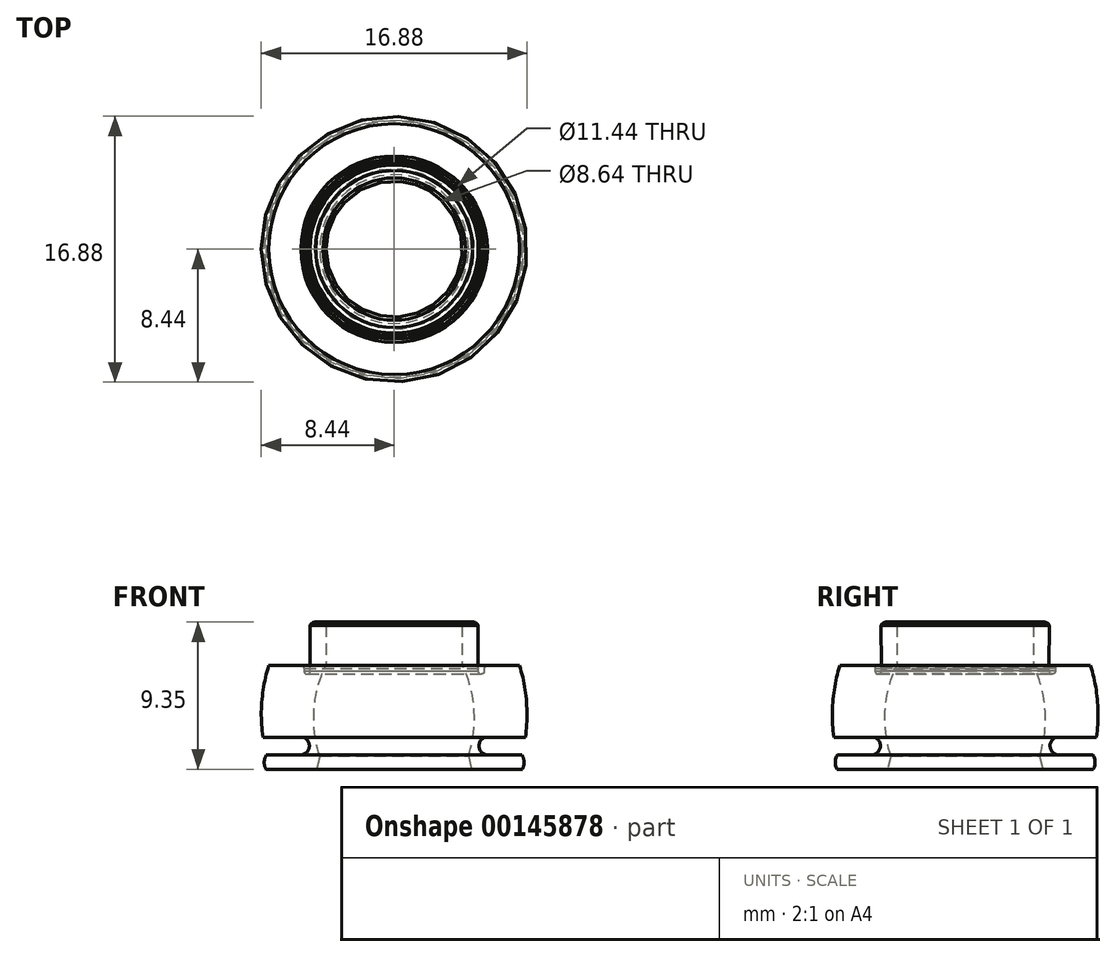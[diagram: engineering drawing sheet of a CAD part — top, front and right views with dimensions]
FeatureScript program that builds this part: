
annotation { "Feature Type Name" : "Feature", "Feature Type Description" : "" }
export const myFeature = defineFeature(function(context is Context, id is Id, definition is map)
    precondition{}
    {
        {
            var Q0;
            Q0=qCreatedBy(makeId("Front.planeOp"),FACE);
            var sketch = newSketch(context, id + "F0", { "sketchPlane" : qUnion([Q0])});
            skLineSegment(sketch, "E0", {"start": v(-10.48, -0.16) * mm, "end": v(-14.05, -0.16) * mm, "construction": true});
            skLineSegment(sketch, "E1", {"start": v(-14.05, 0.64) * mm, "end": v(-10.5, 0.64) * mm, "construction": true});
            skLineSegment(sketch, "E2", {"start": v(-14.05, 2.04) * mm, "end": v(-10.5, 2.04) * mm, "construction": true});
            skLineSegment(sketch, "E3", {"start": v(-10.5, 6.64) * mm, "end": v(-14.05, 6.64) * mm, "construction": true});
            skLineSegment(sketch, "E4", {"start": v(-10.5, 9.34) * mm, "end": v(-14.05, 9.34) * mm, "construction": true});
            skLineSegment(sketch, "E5", {"start": v(-8.1, 0.9) * mm, "end": v(-5.88, 0.9) * mm});
            skPoint(sketch, "E6.endSnap0", {"position": v(-10.51, 4.48) * mm});
            skLineSegment(sketch, "E7", {"start": v(-4.3, 9.15) * mm, "end": v(-4.3, 6.64) * mm});
            skPoint(sketch, "E8", {"position": v(-5.36, 4.42) * mm});
            skPoint(sketch, "E9.visualSharp", {"position": v(-5.36, 2.2) * mm});
            skPoint(sketch, "E10.visualSharp", {"position": v(-5.31, 6.6) * mm});
            skPoint(sketch, "E11.visualSharp", {"position": v(-7.3, 0.86) * mm});
            skLineSegment(sketch, "E12", {"start": v(0.02, -117.65) * mm, "end": v(0.02, -111.65) * mm});
            skLineSegment(sketch, "E13", {"start": v(-8.43, 9.56) * mm, "end": v(-8.43, 0.56) * mm, "construction": true});
            skPoint(sketch, "E13.startSnap0", {"position": v(-8.43, 4.42) * mm});
            skPoint(sketch, "E9.filletArc.center.orphan", {"position": v(-5.4, 2.04) * mm});
            skPoint(sketch, "E14.visualSharp", {"position": v(-5.17, 9.35) * mm});
            skPoint(sketch, "E15.visualSharp", {"position": v(-4.3, 9.35) * mm});
            skArc(sketch, "E15.filletArc", {"start": v(-4.3, 9.15) * mm, "mid": v(-4.36, 9.3) * mm, "end": v(-4.5, 9.35) * mm});
            skLineSegment(sketch, "E16", {"start": v(-8.32, 2.04) * mm, "end": v(-5.74, 2.04) * mm});
            skArc(sketch, "E17", {"start": v(-7.94, 6.61) * mm, "mid": v(-8.38, 4.35) * mm, "end": v(-8.32, 2.04) * mm});
            skLineSegment(sketch, "E18", {"start": v(-8.12, 0) * mm, "end": v(-4.9, 0) * mm});
            skLineSegment(sketch, "E19", {"start": v(-7.94, 6.61) * mm, "end": v(-5.9, 6.61) * mm});
            skLineSegment(sketch, "E20", {"start": v(-5.7, 6.41) * mm, "end": v(-5.7, 6.25) * mm});
            skLineSegment(sketch, "E21", {"start": v(-5.51, 6.05) * mm, "end": v(-5.5, 6.05) * mm});
            skPoint(sketch, "E22.visualSharp", {"position": v(-5.7, 6.61) * mm});
            skArc(sketch, "E22.filletArc", {"start": v(-5.7, 6.41) * mm, "mid": v(-5.77, 6.55) * mm, "end": v(-5.9, 6.61) * mm});
            skLineSegment(sketch, "E23", {"start": v(-5.31, 6.25) * mm, "end": v(-5.32, 9.15) * mm});
            skPoint(sketch, "E24.visualSharp", {"position": v(-5.7, 6.05) * mm});
            skArc(sketch, "E24.filletArc", {"start": v(-5.7, 6.25) * mm, "mid": v(-5.65, 6.1) * mm, "end": v(-5.5, 6.05) * mm});
            skPoint(sketch, "E25.visualSharp", {"position": v(-5.31, 6.05) * mm});
            skArc(sketch, "E25.filletArc", {"start": v(-5.51, 6.05) * mm, "mid": v(-5.37, 6.1) * mm, "end": v(-5.31, 6.25) * mm});
            skArc(sketch, "E26", {"start": v(-4.3, 6.64) * mm, "mid": v(-5.06, 3.78) * mm, "end": v(-4.7, 0.84) * mm});
            skLineSegment(sketch, "E27", {"start": v(-4.97, 9.35) * mm, "end": v(-4.5, 9.35) * mm});
            skArc(sketch, "E28", {"start": v(-5.88, 0.9) * mm, "mid": v(-5.37, 1.42) * mm, "end": v(-5.74, 2.04) * mm});
            skArc(sketch, "E29", {"start": v(-8.1, 0.9) * mm, "mid": v(-8.23, 0.46) * mm, "end": v(-8.12, 0) * mm});
            skArc(sketch, "E30", {"start": v(-4.97, 9.35) * mm, "mid": v(-5.17, 9.3) * mm, "end": v(-5.32, 9.15) * mm});
            skPoint(sketch, "E31", {"position": v(-5.08, 3.33) * mm});
            skLineSegment(sketch, "E32", {"start": v(0, 0) * mm, "end": v(0, 10.46) * mm});
            skLineSegment(sketch, "E33", {"start": v(-4.9, 0) * mm, "end": v(-4.7, 0.84) * mm});
            skSolve(sketch);
        }
        {
            var Q0;
            Q0=makeQuery(id+"F0.imprint","IMPRINT",FACE,{"disambiguationData":[TD([[makeQuery(id+"F0.imprint","IMPRINT",EDGE,{"derivedFrom":sQuery(id+"F0.wireOp",EDGE,"7BqM3D1l-dlXT-mzmC-aZGA-8GqCBN6UsZia")}),-1.0]])]});
            var Q1;
            Q1=makeQuery(id+"F0.imprint","IMPRINT",FACE,{"disambiguationData":[TD([[makeQuery(id+"F0.imprint","IMPRINT",EDGE,{"derivedFrom":sQuery(id+"F0.wireOp",EDGE,"E5")}),-1.0]])]});
            var Q2;
            Q2=sQuery(id+"F0.wireOp",EDGE,"E12");
            revolve(context, id + "F1", {"entities" : qUnion([Q0, Q1]), "axis" : qUnion([Q2]), "revolveType" : RevolveType.FULL});
        }
        {
            var Q0;
            Q0=makeQuery(id+"F1.opRevolve","SWEPT_BODY",BODY,{"disambiguationData":[OSD([sQuery(id+"F0.wireOp",EDGE,"LSrZbnCW-DPXI-OJCB-wGV7-goqquTMaoNQ3"),sQuery(id+"F0.wireOp",EDGE,"E5"),sQuery(id+"F0.wireOp",EDGE,"q9hycEio-vNRm-B8LW-tvsp-It3O9ZgXLD7L"),sQuery(id+"F0.wireOp",EDGE,"E7"),sQuery(id+"F0.wireOp",EDGE,"E11.filletArc"),sQuery(id+"F0.wireOp",EDGE,"E14.filletArc"),sQuery(id+"F0.wireOp",EDGE,"E15.filletArc"),sQuery(id+"F0.wireOp",EDGE,"E16"),sQuery(id+"F0.wireOp",EDGE,"dd15b83b-c64b-43ad-a95b-8cd68dac2268.filletArc"),sQuery(id+"F0.wireOp",EDGE,"zoEumfgO-vDAE-mYGb-WYeo-DXNnPUaAHuwM"),sQuery(id+"F0.wireOp",EDGE,"wh8h3yrd-bVJo-M06d-wALN-6o0yoBlTXFjP"),sQuery(id+"F0.wireOp",EDGE,"NC0weYv5-BuQE-0s04-fJdI-J7ythXOzsNYI"),sQuery(id+"F0.wireOp",EDGE,"E17"),sQuery(id+"F0.wireOp",EDGE,"E18"),sQuery(id+"F0.wireOp",EDGE,"k8CwcPwm-dbJd-xcfX-Vs1Q-rrPQatgC4rnO"),sQuery(id+"F0.wireOp",EDGE,"E19"),sQuery(id+"F0.wireOp",EDGE,"E20"),sQuery(id+"F0.wireOp",EDGE,"E21"),sQuery(id+"F0.wireOp",EDGE,"E22.filletArc"),sQuery(id+"F0.wireOp",EDGE,"E23"),sQuery(id+"F0.wireOp",EDGE,"E24.filletArc"),sQuery(id+"F0.wireOp",EDGE,"E25.filletArc")])]});
            transform(context, id + "F2", {"entities" : qUnion([Q0]), "transformType" : TransformType.TRANSLATION_3D, "dx" : 0.02 * mm, "dy" : 0 * mm, "dz" : -0.1 * mm, "makeCopy" : false});
        }
    });
